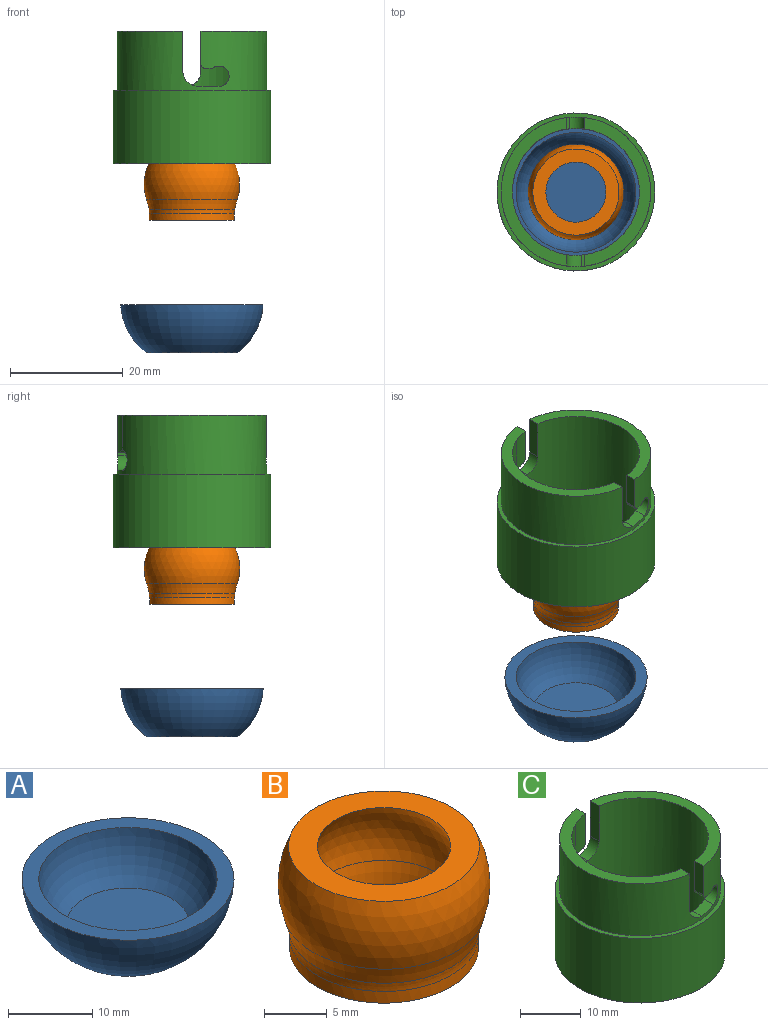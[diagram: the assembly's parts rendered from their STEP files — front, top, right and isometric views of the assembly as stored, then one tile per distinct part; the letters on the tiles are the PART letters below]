
ASSEMBLY  parts=3 mates=2
PART A: 5 faces, bbox 25.2x25.2x8.5 mm
  f0: plane 16.05x16.05mm, normal (0,0,-1), area 202.4mm2, adj f1
  f1: torus R=1.21mm, axis (0,0,-1), area 686mm2, adj f0,f2
  f2: plane 25.23x25.23mm, normal (0,0,1), area 146.2mm2, adj f1,f4
  f3: plane 14.66x14.66mm, normal (0,0,1), area 168.8mm2, adj f4
  f4: torus R=1.21mm, axis (0,0,-1), area 441.7mm2, adj f2,f3
PART B: 10 faces, bbox 23.2x23.2x12.5 mm
  f0: plane 13.04x13.04mm, normal (0,0,-1), area 37.8mm2, adj f5,f6
  f1: sphere r=8.47mm, area 338.5mm2, adj f2,f3
  f2: torus R=18.67mm, axis (0,0,-1), area 84.9mm2, adj f1,f9
  f3: plane 15.27x15.27mm, normal (0,0,1), area 93.8mm2, adj f1,f4
  f4: sphere r=6.47mm, area 232.7mm2, adj f3,f5
  f5: torus R=18.67mm, axis (0,0,-1), area 104.5mm2, adj f0,f4
  f6: cylinder r=6.52mm len=13.04mm, axis (0,0,1), area 61.4mm2, adj f0,f8
  f7: cylinder r=7.53mm len=15.06mm, axis (0,0,1), area 53.6mm2, adj f8,f9
  f8: plane 15.06x15.06mm, normal (0,0,-1), area 44.7mm2, adj f6,f7
  f9: torus R=12.61mm, axis (0,0,1), area 40.9mm2, adj f2,f7
PART C: 23 faces, bbox 28x28x23.5 mm
  f0: cylinder r=11.25mm len=23.5mm, axis (0,0,-1), area 1545.4mm2, adj f1,f4,f5,f6,f9,f10,f11,f12
  f1: cylinder r=11.25mm len=6.6mm, axis (0,0,-1), area 21.7mm2, adj f0,f5,f17,f18,f20,f22
  f2: cylinder r=13.25mm len=26.5mm, axis (0,0,-1), area 759.6mm2, adj f3,f4,f5,f8,f9,f10,f11,f12
  f3: cylinder r=13.25mm len=6.6mm, axis (0,0,-1), area 21.4mm2, adj f2,f5,f17,f18,f20,f22
  f4: plane 26.31x11.65mm, normal (0,0,1), area 70.6mm2, adj f0,f2,f13,f19
  f5: plane 26.31x11.65mm, normal (0,0,1), area 70.6mm2, adj f0,f1,f2,f3,f12,f20
  f6: plane 28x28mm, normal (0,0,-1), area 218.1mm2, adj f0,f7
  f7: cylinder r=14mm len=28mm, axis (0,0,-1), area 1143.5mm2, adj f6,f8
  f8: plane 28x28mm, normal (0,0,1), area 64.2mm2, adj f2,f7
  f9: plane 3.74x3.03mm, normal (0,0,1), area 7.8mm2, adj f0,f2,f10,f14
  f10: cylinder r=1.8mm len=3.62mm, axis (0,1,0), area 15.6mm2, adj f0,f2,f9,f11
  f11: plane 2.41x1.34mm, normal (0,0,-1), area 2.8mm2, adj f0,f2,f10,f15
  f12: plane 7.14x2.02mm, normal (1,0,0), area 14.4mm2, adj f0,f2,f5,f14
  f13: plane 5.88x2.02mm, normal (-1,0,0), area 11.9mm2, adj f0,f2,f4,f15
  f14: cylinder r=2.66mm len=2.66mm, axis (0,-1,0), area 8.4mm2, adj f0,f2,f9,f12
  f15: cylinder r=0.72mm len=2.15mm, axis (0,1,0), area 2.3mm2, adj f0,f2,f11,f13
  f16: plane 3.74x3.03mm, normal (0,0,1), area 7.8mm2, adj f0,f2,f17,f21
  f17: cylinder r=1.8mm len=3.62mm, axis (0,-1,0), area 15.6mm2, adj f0,f1,f2,f3,f16,f18
  f18: plane 2.41x1.34mm, normal (0,0,-1), area 2.8mm2, adj f1,f3,f17,f22
  f19: plane 7.14x2.02mm, normal (-1,0,0), area 14.4mm2, adj f0,f2,f4,f21
  f20: plane 5.88x2.02mm, normal (1,0,0), area 11.9mm2, adj f1,f3,f5,f22
  f21: cylinder r=2.66mm len=2.66mm, axis (0,1,0), area 8.4mm2, adj f0,f2,f16,f19
  f22: cylinder r=0.72mm len=2.15mm, axis (0,-1,0), area 2.3mm2, adj f1,f3,f18,f20
PLACE A t=(-30.03,11.11,-13.14)mm fixed
PLACE B rot(axis=(0,-0.01,-1),0deg) t=(-30.03,11.11,-13.14)mm
PLACE C rot(axis=(0,-0.01,-1),0deg) t=(19.97,11.11,20.4)mm
MATE revolute C.f7 <-> B.f2  axis (0,0,-1) through (19.97,11.11,20.4)mm
MATE cylindrical B.f2 <-> A.f1  axis (0,0,-1) through (19.97,11.11,11.86)mm
